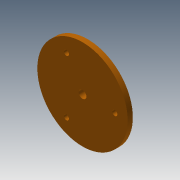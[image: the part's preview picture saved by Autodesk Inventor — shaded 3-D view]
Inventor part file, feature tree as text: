
AUTODESK INVENTOR PART (.ipt)
format: ipt  version: 2015 (Build 190159000, 159)  size: 111,104 bytes
history: native  units: mm
features: extrude x4, sketch x4
ambient origin geometry x8: Origin, YZ Plane, XZ Plane, XY Plane, X Axis, Y Axis, Z Axis, Center Point
bodies: Solid1 (feature_tree)
feature tree (8):
  extrude  "Extrusion1"  Depth=3.0mm
  extrude  "Extrusion2"  Depth=10.0mm
  extrude  "Extrusion3"  Depth=3.8mm
  extrude  "Extrusion4"  Depth=2.0mm
  sketch  "Sketch1"  dims[d0=35.0mm d1=3.0mm]
  sketch  "Sketch2"  dims[d2=2.0mm d3=0.0mm d4=10.0mm]
  sketch  "Sketch3"  dims[d5=3.8mm d6=0.0mm d7=6.0mm]
  sketch  "Sketch4"  dims[d8=3.8mm d9=0.0mm d11=2.0mm d12=120.0deg d13=120.0deg d14=2.0mm d15=2.0mm d16=3.8mm d17=0.0mm]
